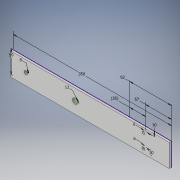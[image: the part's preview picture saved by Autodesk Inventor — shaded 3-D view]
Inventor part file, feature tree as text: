
AUTODESK INVENTOR PART (.ipt)
format: ipt  version: 2019 (Build 230136000, 136)  size: 111,616 bytes
history: native  units: mm
features: extrude x2, sketch x1
ambient origin geometry x8: Origin, YZ Plane, XZ Plane, XY Plane, X Axis, Y Axis, Z Axis, Center Point
bodies: Solid1 (feature_tree)
feature tree (3):
  sketch  "Sketch1"  dims[d0=350.0mm d1=50.0mm d2=6.0mm d3=6.0mm d4=10.0mm d5=10.0mm d6=57.0mm d7=92.0mm d8=35.0mm d9=5.0mm d10=0.0mm d11=12.0mm d12=8.0mm d13=5.0mm d14=0.0mm]
  extrude  "Extrusion1"  Depth=50.0mm
  extrude  "Extrusion2"  Depth=6.0mm
